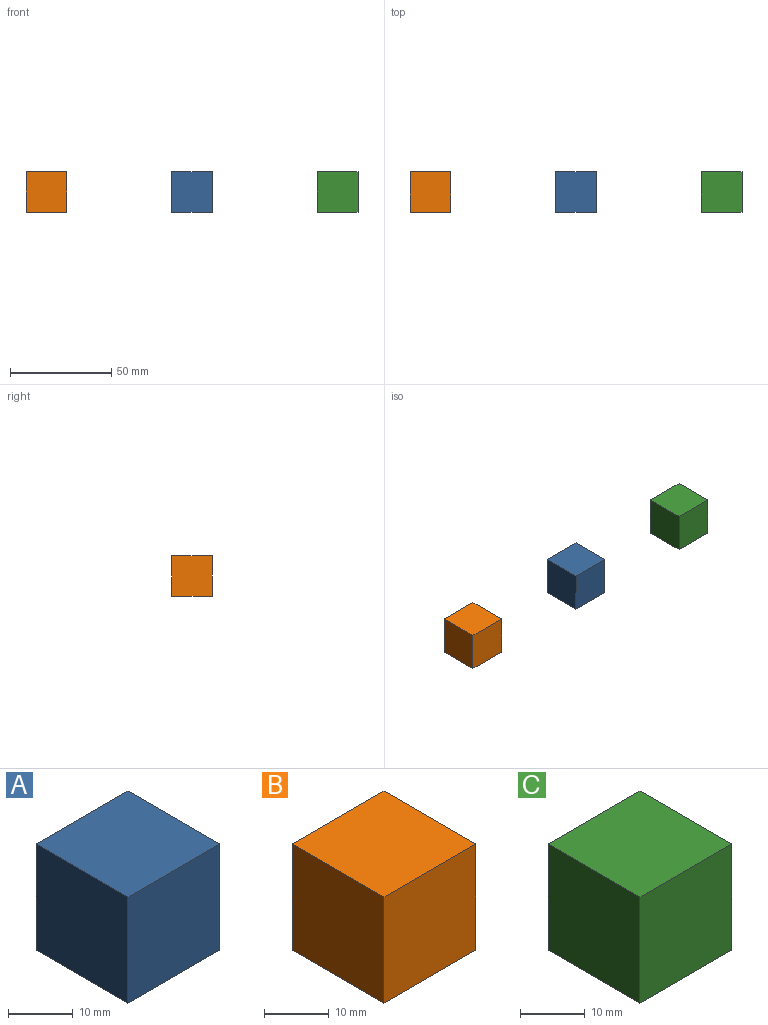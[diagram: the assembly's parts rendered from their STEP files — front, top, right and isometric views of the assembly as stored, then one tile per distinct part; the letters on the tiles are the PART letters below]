
ASSEMBLY  parts=3 mates=2
PART A: 6 faces, bbox 20x20x20 mm
  f0: plane 20x20mm, normal (-1,0,0), area 400mm2, adj f1,f3,f4,f5
  f1: plane 20x20mm, normal (0,0,-1), area 400mm2, adj f0,f2,f4,f5
  f2: plane 20x20mm, normal (1,0,0), area 400mm2, adj f1,f3,f4,f5
  f3: plane 20x20mm, normal (0,0,1), area 400mm2, adj f0,f2,f4,f5
  f4: plane 20x20mm, normal (0,-1,0), area 400mm2, adj f0,f1,f2,f3
  f5: plane 20x20mm, normal (0,1,0), area 400mm2, adj f0,f1,f2,f3
PART B: 6 faces, bbox 20x20x20 mm
  f0: plane 20x20mm, normal (-1,0,0), area 400mm2, adj f1,f3,f4,f5
  f1: plane 20x20mm, normal (0,0,-1), area 400mm2, adj f0,f2,f4,f5
  f2: plane 20x20mm, normal (1,0,0), area 400mm2, adj f1,f3,f4,f5
  f3: plane 20x20mm, normal (0,0,1), area 400mm2, adj f0,f2,f4,f5
  f4: plane 20x20mm, normal (0,-1,0), area 400mm2, adj f0,f1,f2,f3
  f5: plane 20x20mm, normal (0,1,0), area 400mm2, adj f0,f1,f2,f3
PART C: 6 faces, bbox 20x20x20 mm
  f0: plane 20x20mm, normal (-1,0,0), area 400mm2, adj f1,f3,f4,f5
  f1: plane 20x20mm, normal (0,0,-1), area 400mm2, adj f0,f2,f4,f5
  f2: plane 20x20mm, normal (1,0,0), area 400mm2, adj f1,f3,f4,f5
  f3: plane 20x20mm, normal (0,0,1), area 400mm2, adj f0,f2,f4,f5
  f4: plane 20x20mm, normal (0,-1,0), area 400mm2, adj f0,f1,f2,f3
  f5: plane 20x20mm, normal (0,1,0), area 400mm2, adj f0,f1,f2,f3
PLACE A t=(-22.16,43.43,-22.14)mm
PLACE B t=(-114.12,43.43,-22.14)mm
PLACE C t=(69.79,43.43,-22.14)mm
MATE slider A.f2 <-> B.f0  axis (1,0,0) through (17.84,33.43,-12.14)mm
MATE slider C.f2 <-> A.f0  axis (1,0,0) through (89.79,33.43,-12.14)mm
